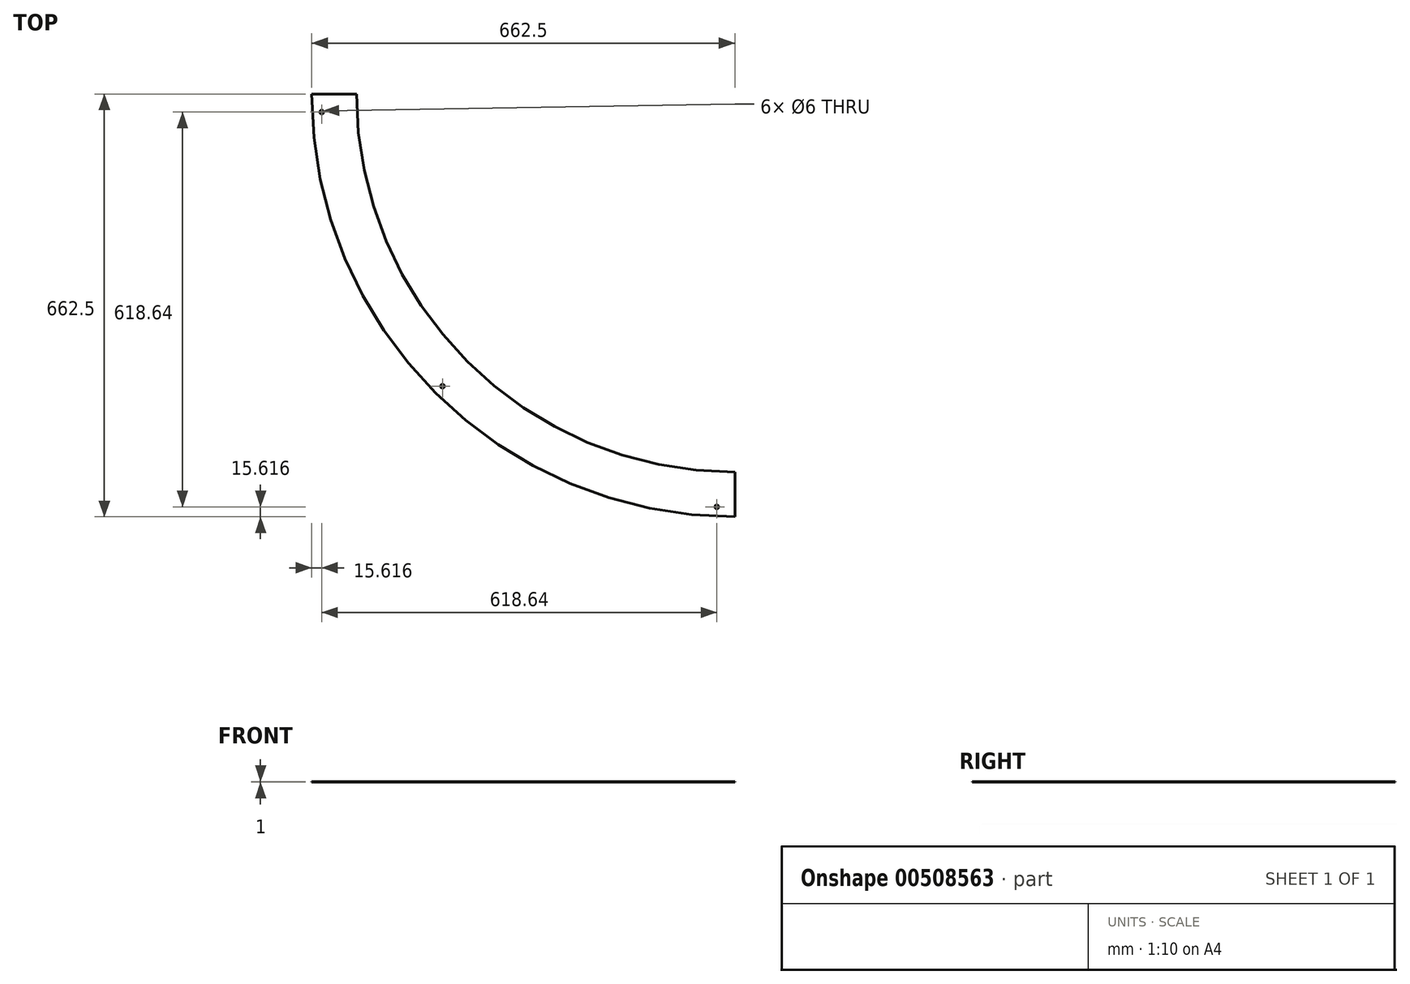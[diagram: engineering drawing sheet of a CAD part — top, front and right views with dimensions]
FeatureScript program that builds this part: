
annotation { "Feature Type Name" : "Feature", "Feature Type Description" : "" }
export const myFeature = defineFeature(function(context is Context, id is Id, definition is map)
    precondition{}
    {
        {
            var Q0;
            Q0=qCreatedBy(makeId("Top.planeOp"),FACE);
            var sketch = newSketch(context, id + "F0", { "sketchPlane" : qUnion([Q0])});
            skArc(sketch, "E0", {"start": v(-592.5, 0) * mm, "mid": v(-418.96, -418.96) * mm, "end": v(0, -592.5) * mm});
            skArc(sketch, "E1", {"start": v(-662.5, 0) * mm, "mid": v(-468.46, -468.46) * mm, "end": v(0, -662.5) * mm});
            skLineSegment(sketch, "E2", {"start": v(-662.5, 0) * mm, "end": v(-592.5, 0) * mm});
            skLineSegment(sketch, "E3", {"start": v(0, -592.5) * mm, "end": v(0, -662.5) * mm});
            skSolve(sketch);
        }
        {
            var Q0;
            Q0=makeQuery(id+"F0.imprint","IMPRINT",FACE,{"disambiguationData":[TD([[makeQuery(id+"F0.imprint","IMPRINT",EDGE,{"derivedFrom":sQuery(id+"F0.wireOp",EDGE,"E0")}),-1.0]])]});
            var sketch = newSketch(context, id + "F1", { "sketchPlane" : qUnion([Q0])});
            skPoint(sketch, "E4", {"position": v(-646.88, -28.24) * mm});
            skPoint(sketch, "E5", {"position": v(-457.85, -457.85) * mm});
            skPoint(sketch, "E6", {"position": v(-28.24, -646.88) * mm});
            skArc(sketch, "E7", {"start": v(-646.88, -28.24) * mm, "mid": v(-457.85, -457.85) * mm, "end": v(-28.24, -646.88) * mm, "construction": true});
            skLineSegment(sketch, "E8", {"start": v(-646.88, -28.24) * mm, "end": v(0, 0) * mm, "construction": true});
            skLineSegment(sketch, "E9", {"start": v(-28.24, -646.88) * mm, "end": v(0, 0) * mm, "construction": true});
            skLineSegment(sketch, "E10", {"start": v(-457.85, -457.85) * mm, "end": v(0, 0) * mm, "construction": true});
            skSolve(sketch);
        }
        {
            var Q0;
            Q0=makeQuery(id+"F0.imprint","IMPRINT",FACE,{"disambiguationData":[TD([[makeQuery(id+"F0.imprint","IMPRINT",EDGE,{"derivedFrom":sQuery(id+"F0.wireOp",EDGE,"E0")}),-1.0]])]});
            extrude(context, id + "F2", {"entities" : qUnion([Q0]), "oppositeDirection" : true, "depth" : 1 * mm});
        }
        {
            var Q0;
            Q0=makeQuery(id+"F0.imprint","IMPRINT",FACE,{"disambiguationData":[TD([[makeQuery(id+"F0.imprint","IMPRINT",EDGE,{"derivedFrom":sQuery(id+"F0.wireOp",EDGE,"E0")}),-1.0]])]});
            var sketch = newSketch(context, id + "F3", { "sketchPlane" : qUnion([Q0])});
            skCircle(sketch, "E11", {"center": v(-646.88, -28.24) * mm, "radius": 3 * mm});
            skCircle(sketch, "E12", {"center": v(-28.24, -646.88) * mm, "radius": 3 * mm});
            skCircle(sketch, "E13", {"center": v(-457.85, -457.85) * mm, "radius": 3 * mm});
            skSolve(sketch);
        }
        {
            var Q0;
            Q0 = qSketchRegion(id + "F3", true);
            extrude(context, id + "F4", {"entities" : qUnion([Q0]), "operationType" : NewBodyOperationType.REMOVE, "endBound" : BoundingType.THROUGH_ALL, "oppositeDirection" : true, "depth" : 25 * mm});
        }
    });
